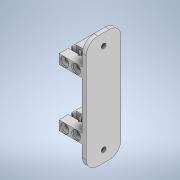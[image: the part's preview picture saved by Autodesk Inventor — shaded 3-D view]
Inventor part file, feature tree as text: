
AUTODESK INVENTOR PART (.ipt)
format: ipt  version: 2020 (Build 240168000, 168)  size: 451,584 bytes
history: native  units: mm
features: other x4, extrude x3, sketch x3, fillet x1, mirror x1, projected_geometry x1
ambient origin geometry x8: Origin, YZ Plane, XZ Plane, XY Plane, X Axis, Y Axis, Z Axis, Center Point
bodies: Solide1 (feature_tree)
feature tree (13):
  other  "servo_holder.ipt"
  extrude  "Extrusion1"  Depth=10.0mm
  extrude  "Extrusion2"  Depth=1.0mm TaperAngle=0.0deg
  fillet  "Congé1"  Radius=20.0mm
  extrude  "Extrusion3"  Depth=10.0mm
  other  "Plan de construction2"
  mirror  "Symétrie1"
  other  "Solide1::servo_holder.ipt"
  other  "FonctionRepérage1"
  sketch  "Esquisse1"
  projected_geometry  "Boucle projetée1"
  sketch  "Esquisse2"
  sketch  "Esquisse3"
